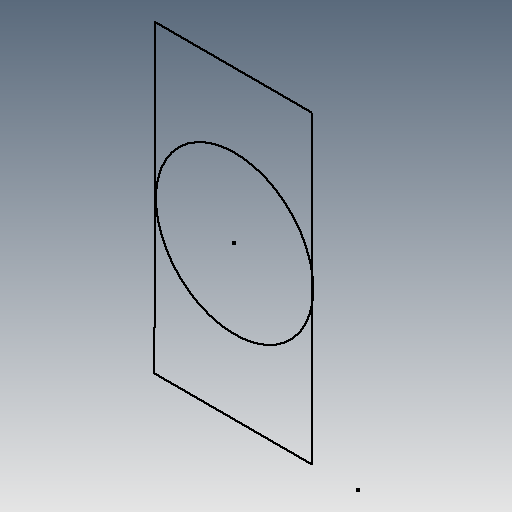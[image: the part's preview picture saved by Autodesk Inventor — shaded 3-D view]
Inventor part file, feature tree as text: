
AUTODESK INVENTOR PART (.ipt)
format: ipt  version: 2017 (Build 210142000, 142)  size: 71,680 bytes
history: native  units: in
note: dims shown in document units (in); Inventor stores cm internally (conversion verified against a paired STEP export)
features: sketch x1
ambient origin geometry x8: Origin, YZ Plane, XZ Plane, XY Plane, X Axis, Y Axis, Z Axis, Center Point
feature tree (1):
  sketch  "Sketch1"
